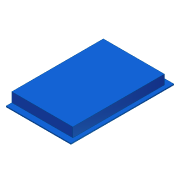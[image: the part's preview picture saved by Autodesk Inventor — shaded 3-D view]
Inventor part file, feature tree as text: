
AUTODESK INVENTOR PART (.ipt)
format: ipt  version: 2012 (Build 160160000, 160)  size: 86,016 bytes
history: native  units: in
note: dims shown in document units (in); Inventor stores cm internally (conversion verified against a paired STEP export)
features: extrude x2, sketch x2
ambient origin geometry x8: Origin, YZ Plane, XZ Plane, XY Plane, X Axis, Y Axis, Z Axis, Center Point
bodies: Solid1 (feature_tree)
feature tree (4):
  extrude  "Extrusion1"  Depth=17.0in
  extrude  "Extrusion2"  Depth=1.0in
  sketch  "Sketch1"  dims[d0=2.75in d1=17.0in]
  sketch  "Sketch2"  dims[d2=0.25in d3=1.0in d4=27.0in d5=0.0in d6=0.25in d7=1.5in d8=27.0in d9=0.0in]
